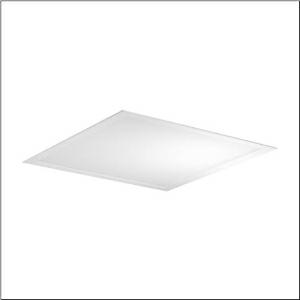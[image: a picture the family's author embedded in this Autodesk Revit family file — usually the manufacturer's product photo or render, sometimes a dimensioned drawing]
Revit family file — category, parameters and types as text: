
# Revit family: apollon_21_square_51mq11w72314
name_source: partatom
category: Lighting Fixtures
units: mm (PartAtom-declared; Revit-internal decimal feet)

## family parameters
Cut with Voids When Loaded = No
Host = Face
Light Source = No
Part Type = Normal
Room Calculation Point = No
Round Connector Dimension = Use Diameter
Shared = No

## types (1)
- Apollon 21 square (1 x LED, 4100 lm, 23.3 W, 3000K)
    Apparent Load = 23 VA
    CIE Flux Codes = 60 87 97 100 100
    Color Rendering = 80
    Color Temperature = 3000K
    Default Elevation = 1800 mm
    Description = Apollon 21 square, office luminaire, primary optical cover: micro prismatic cover, of PMMA, CAT 2 (L<= 3000cd/m²), light emission: direct distribution, primary light characteristic: symmetric, installation type: lay-in mounting, LED, rated luminous flux: 4.100lm, luminous efficacy: 176lm/W, light colour: 830, colour temperature: 3000K, control gear: ON/OFF, with terminal, 3-pole, mains connection: 220..240V, AC/DC, 0/50..60Hz, rated input power: 23.3W, suitable for self-contained emergency lighting element 59MQE002602A with integrated self-test function according to EN 60598-2-22, housing, of aluminium, coated, traffic white (RAL 9016), module: M625, length: 620mm, width: 620mm, height: 55mm, recess depth: 180mm, housing upper side, of sheet steel, galvanised, protection rating (complete): IP20, protection rating (lamp compartment, on room side): IP50, insulation class (complete): insulation class II (safety insulation), certification: CE, ENEC, impact resistance: IK03, permissible operating ambient temperature: -20..+45°C, permissible storage temperature: -40..+80°C, standard: EN 60598-2-22, packaging unit: 1 piece
    Height = 0 mm  [stored 0 ft]
    Lamp = 1 x LED
    Lamp Light Flux = 4100 lm
    Lamp Power = 23.3 W
    Lamp count = 1
    Length = 620 mm
    Luminous efficacy = 176 lm/W
    Manufacturer = Siteco
    ModVariant = No
    Model = 51MQ11W72314
    Mounting Place = Ceiling
    Mounting Type = Recessed
    Number of Poles = 1
    OnlyDefault = Yes
    Power Factor = 1
    Product Name = Apollon 21 square
    Product group = office luminaire | ceiling recessed
    ProductGroupID = 400
    Protection Class = Protection class II
    Protection Degree = IP 20
    RLX_Detail_Level = 1
    RLX_Emergency_Light_Flux = 0 lm
    RLX_Emergency_Type = 0
    RLX_Emergency_Type_DB = No
    RlxData = <blob elided: 13157 chars, md5=e26ec87e>
    Socket = socket
    Standby Power = 0 W
    System Light Flux = 4100 lm
    System Power = 23 W
    Type Comments = Product without accessories
    Type Image = l_1291054.jpg
    URL = http://relux.com
    VarID = ---
    Voltage = 0 V
    Weight = 0.00 kg
    Width = 620 mm

note: [stored X ft] marks values corroborated as IEEE doubles in the binary element streams (Revit-internal decimal feet)

## geometry (parser evidence)
native form markers: Sweep x10
no freeform markers — native parametric forms only
